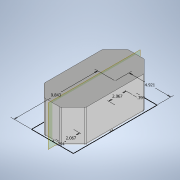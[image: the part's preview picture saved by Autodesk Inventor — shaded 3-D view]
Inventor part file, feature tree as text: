
AUTODESK INVENTOR PART (.ipt)
format: ipt  version: 2020 (Build 240168000, 168)  size: 194,048 bytes
history: native  units: in
note: dims shown in document units (in); Inventor stores cm internally (conversion verified against a paired STEP export)
features: sketch x3, extrude x3, fillet x2, hole x1, plane x1, mirror x1, chamfer x1
ambient origin geometry x8: Origin, YZ Plane, XZ Plane, XY Plane, X Axis, Y Axis, Z Axis, Center Point
bodies: Solid1 (feature_tree)
feature tree (12):
  sketch  "Sketch1"  dims[d0=4.9213in d1=9.8425in]
  extrude  "Extrusion1"  Depth=9.8425in
  hole  "Hole1"  [1 undecoded]
  extrude  "Extrusion2"  Depth=2.067in
  extrude  "Extrusion3"  Depth=3.937in TaperAngle=0.0deg
  fillet  "Fillet2"  Radius=0.25in
  plane  "Work Plane1"
  mirror  "Mirror1"
  chamfer  "Chamfer1"  Distance=0.5in
  fillet  "Fillet1"  Radius=0.125in
  sketch  "Sketch2"  dims[d2=0.3937in d3=2.0669in]
  sketch  "Sketch3"  dims[d4=0.3937in d5=2.067in d6=3.937in d7=0.0in d8=4.1339in d9=0.75in d10=0.375in d11=0.25in d12=0.5635in d13=3.5433in d14=0.0in d15=0.25in d16=0.5in d17=0.125in d18=0.5in d19=0.25in d20=0.125in d21=0.25in d22=0.0in d23=0.5in d24=0.125in d25=0.0in d26=0.125in d27=1.5in d28=0.125in d29=45.0deg]
note: 1 required parameter value undecoded (feature->parameter linkage not recoverable at this tier; creation-order binding heuristic only, values carry confidence <= 0.55)
